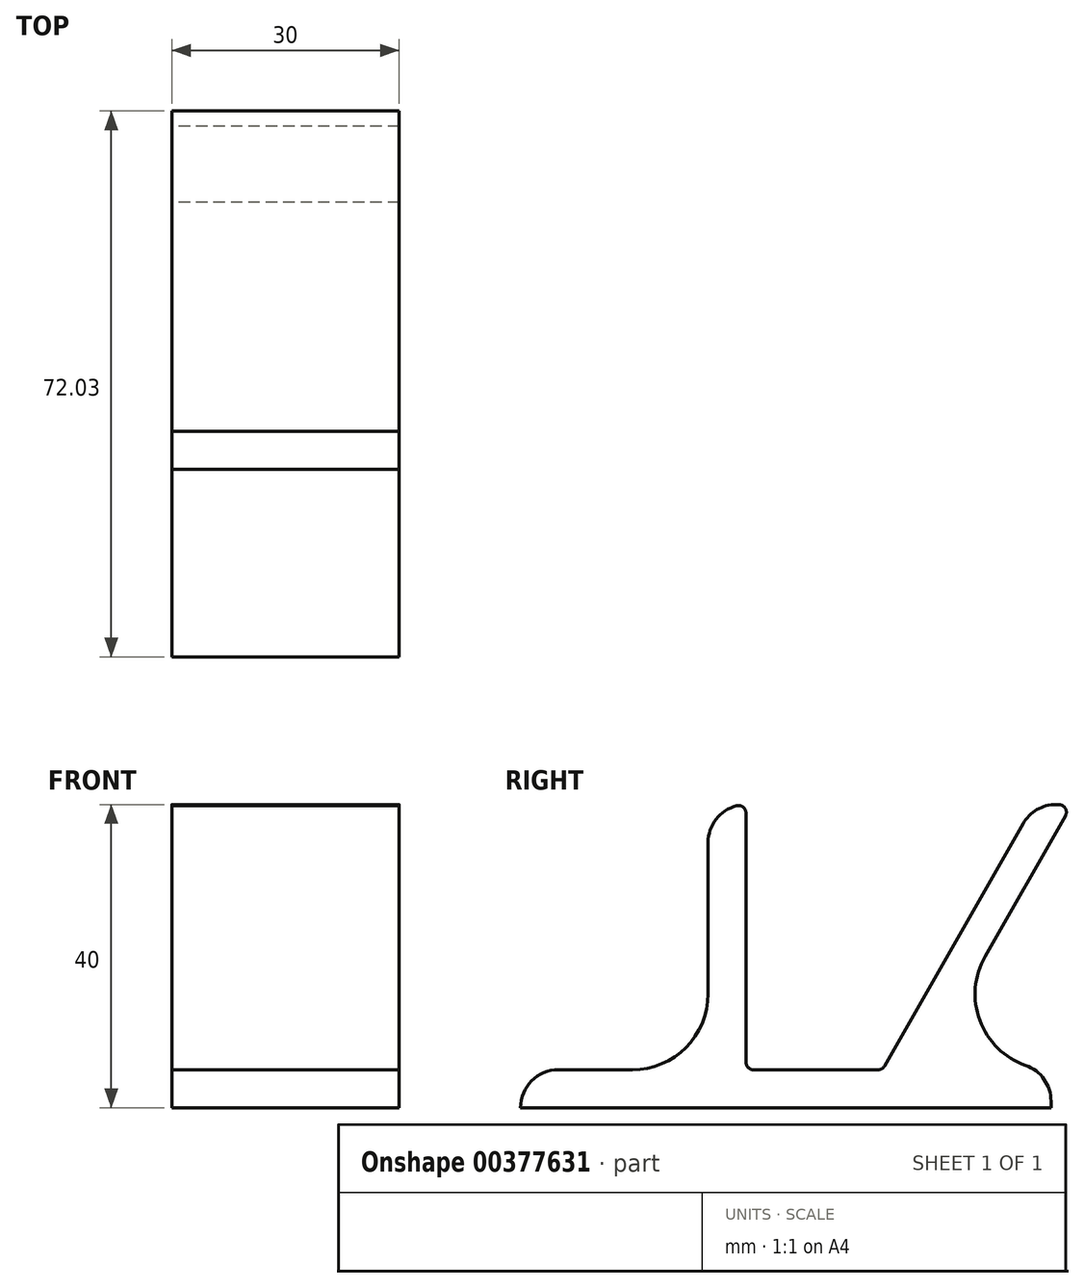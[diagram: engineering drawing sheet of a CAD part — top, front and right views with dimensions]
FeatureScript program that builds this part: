
annotation { "Feature Type Name" : "Feature", "Feature Type Description" : "" }
export const myFeature = defineFeature(function(context is Context, id is Id, definition is map)
    precondition{}
    {
        {
            var Q0;
            Q0=qCreatedBy(makeId("Right.planeOp"),FACE);
            var sketch = newSketch(context, id + "F0", { "sketchPlane" : qUnion([Q0])});
            skLineSegment(sketch, "E0", {"start": v(-27.06, 0) * mm, "end": v(42.94, 0) * mm});
            skLineSegment(sketch, "E1", {"start": v(42.94, 0) * mm, "end": v(42.94, 5) * mm});
            skLineSegment(sketch, "E2", {"start": v(42.94, 5) * mm, "end": v(25.7, 5) * mm});
            skLineSegment(sketch, "E3", {"start": v(45.7, 40) * mm, "end": v(40.7, 40) * mm});
            skLineSegment(sketch, "E4", {"start": v(20.7, 5) * mm, "end": v(2.7, 5) * mm});
            skLineSegment(sketch, "E5", {"start": v(2.7, 5) * mm, "end": v(2.7, 40) * mm});
            skLineSegment(sketch, "E6", {"start": v(2.7, 40) * mm, "end": v(-2.3, 40) * mm});
            skLineSegment(sketch, "E7", {"start": v(-2.3, 40) * mm, "end": v(-2.3, 5) * mm});
            skLineSegment(sketch, "E8", {"start": v(-2.3, 5) * mm, "end": v(-27.3, 5) * mm});
            skLineSegment(sketch, "E9", {"start": v(-27.3, 5) * mm, "end": v(-27.06, 0) * mm});
            skLineSegment(sketch, "E10", {"start": v(20.7, 5) * mm, "end": v(40.7, 40) * mm});
            skLineSegment(sketch, "E11", {"start": v(45.7, 40) * mm, "end": v(25.7, 5) * mm});
            skLineSegment(sketch, "E12.trimOffspring", {"start": v(20.7, 5) * mm, "end": v(8.89, 5) * mm});
            skSolve(sketch);
        }
        {
            var Q0;
            Q0=makeQuery(id+"F0.imprint","IMPRINT",FACE,{"disambiguationData":[TD([[makeQuery(id+"F0.imprint","IMPRINT",EDGE,{"derivedFrom":sQuery(id+"F0.wireOp",EDGE,"E0")}),1.0]])]});
            extrude(context, id + "F1", {"entities" : qUnion([Q0]), "depth" : 30 * mm});
        }
        {
            var Q0;
            Q0=makeQuery(id+"F1.opExtrude","SWEPT_EDGE",EDGE,{"disambiguationData":[OSD([sQuery(id+"F0.wireOp",EDGE,"E2"),sQuery(id+"F0.wireOp",EDGE,"E11")])]});
            var Q1;
            Q1=makeQuery(id+"F1.opExtrude","SWEPT_EDGE",EDGE,{"disambiguationData":[OSD([sQuery(id+"F0.wireOp",EDGE,"E7"),sQuery(id+"F0.wireOp",EDGE,"E8")])]});
            fillet(context, id + "F2", {"entities" : qUnion([Q0, Q1]), "radius" : 10 * mm, "tangentPropagation" : true, "allowEdgeOverflow" : false});
        }
        {
            var Q0;
            Q0=makeQuery(id+"F1.opExtrude","SWEPT_EDGE",EDGE,{"disambiguationData":[OSD([sQuery(id+"F0.wireOp",EDGE,"E8"),sQuery(id+"F0.wireOp",EDGE,"E9")])]});
            var Q1;
            Q1=makeQuery(id+"F1.opExtrude","SWEPT_EDGE",EDGE,{"disambiguationData":[OSD([sQuery(id+"F0.wireOp",EDGE,"E1"),sQuery(id+"F0.wireOp",EDGE,"E2")])]});
            var Q2;
            Q2=makeQuery(id+"F1.opExtrude","SWEPT_EDGE",EDGE,{"disambiguationData":[OSD([sQuery(id+"F0.wireOp",EDGE,"E3"),sQuery(id+"F0.wireOp",EDGE,"E10")])]});
            var Q3;
            Q3=makeQuery(id+"F1.opExtrude","SWEPT_EDGE",EDGE,{"disambiguationData":[OSD([sQuery(id+"F0.wireOp",EDGE,"E6"),sQuery(id+"F0.wireOp",EDGE,"E7")])]});
            fillet(context, id + "F3", {"entities" : qUnion([Q0, Q1, Q2, Q3]), "radius" : 5 * mm, "tangentPropagation" : true, "allowEdgeOverflow" : false});
        }
        {
            var Q0;
            Q0=makeQuery(id+"F1.opExtrude","SWEPT_EDGE",EDGE,{"disambiguationData":[OSD([sQuery(id+"F0.wireOp",EDGE,"E4"),sQuery(id+"F0.wireOp",EDGE,"E5")])]});
            var Q1;
            Q1=makeQuery(id+"F1.opExtrude","SWEPT_EDGE",EDGE,{"disambiguationData":[OSD([sQuery(id+"F0.wireOp",EDGE,"E10"),sQuery(id+"F0.wireOp",EDGE,"E12.trimOffspring")])]});
            var Q2;
            Q2=makeQuery(id+"F3.opFillet","BLEND_EDGE",EDGE,{"blendedFrom":[makeQuery(id+"F1.opExtrude","SWEPT_EDGE",EDGE,{"disambiguationData":[OSD([sQuery(id+"F0.wireOp",EDGE,"E6"),sQuery(id+"F0.wireOp",EDGE,"E7")])]}),makeQuery(id+"F1.opExtrude","SWEPT_FACE",FACE,{"disambiguationData":[OSD([sQuery(id+"F0.wireOp",EDGE,"E5")])]})],"blendedInto":[makeQuery(id+"F1.opExtrude","SWEPT_FACE",FACE,{"disambiguationData":[OSD([sQuery(id+"F0.wireOp",EDGE,"E5")])]})]});
            var Q3;
            Q3=makeQuery(id+"F1.opExtrude","SWEPT_EDGE",EDGE,{"disambiguationData":[OSD([sQuery(id+"F0.wireOp",EDGE,"E3"),sQuery(id+"F0.wireOp",EDGE,"E11")])]});
            fillet(context, id + "F4", {"entities" : qUnion([Q0, Q1, Q2, Q3]), "radius" : 1 * mm, "tangentPropagation" : true, "allowEdgeOverflow" : false});
        }
    });
